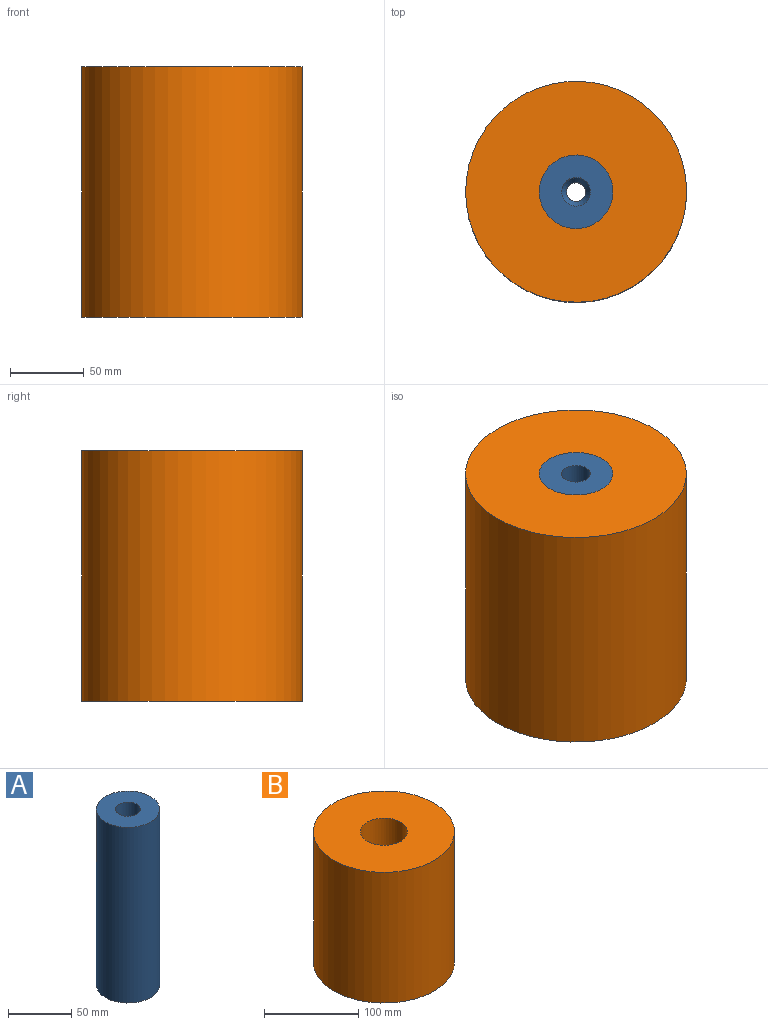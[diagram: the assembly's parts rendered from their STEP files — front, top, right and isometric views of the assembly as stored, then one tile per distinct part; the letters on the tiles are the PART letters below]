
ASSEMBLY  parts=2 mates=1
PART A: 6 faces, bbox 50x50x170.1 mm
  f0: plane 50x50mm, normal (0,0,1), area 1664.8mm2, adj f1,f5
  f1: cylinder r=9.75mm len=103.9mm, axis (0,0,-1), area 6365mm2, adj f0,f2
  f2: cone r=6.4mm half-angle=30deg, axis (0,0,1), area 339.9mm2, adj f1,f3
  f3: cylinder r=6.4mm len=60.4mm, axis (0,0,-1), area 2428.7mm2, adj f2,f4
  f4: plane 50x50mm, normal (0,0,-1), area 1834.8mm2, adj f3,f5
  f5: cylinder r=25mm len=170.1mm, axis (0,0,-1), area 26719.2mm2, adj f0,f4
PART B: 4 faces, bbox 150x150x170.1 mm
  f0: plane 150x150mm, normal (0,0,1), area 15708mm2, adj f1,f3
  f1: cylinder r=25mm len=170.1mm, axis (0,0,-1), area 26719.2mm2, adj f0,f2
  f2: plane 150x150mm, normal (0,0,-1), area 15708mm2, adj f1,f3
  f3: cylinder r=75mm len=170.1mm, axis (0,0,-1), area 80157.7mm2, adj f0,f2
PLACE A at identity fixed
PLACE B at identity
MATE fastened B.f1 <-> A.f1  axis (0,0,-1) through (0,0,170.1)mm
